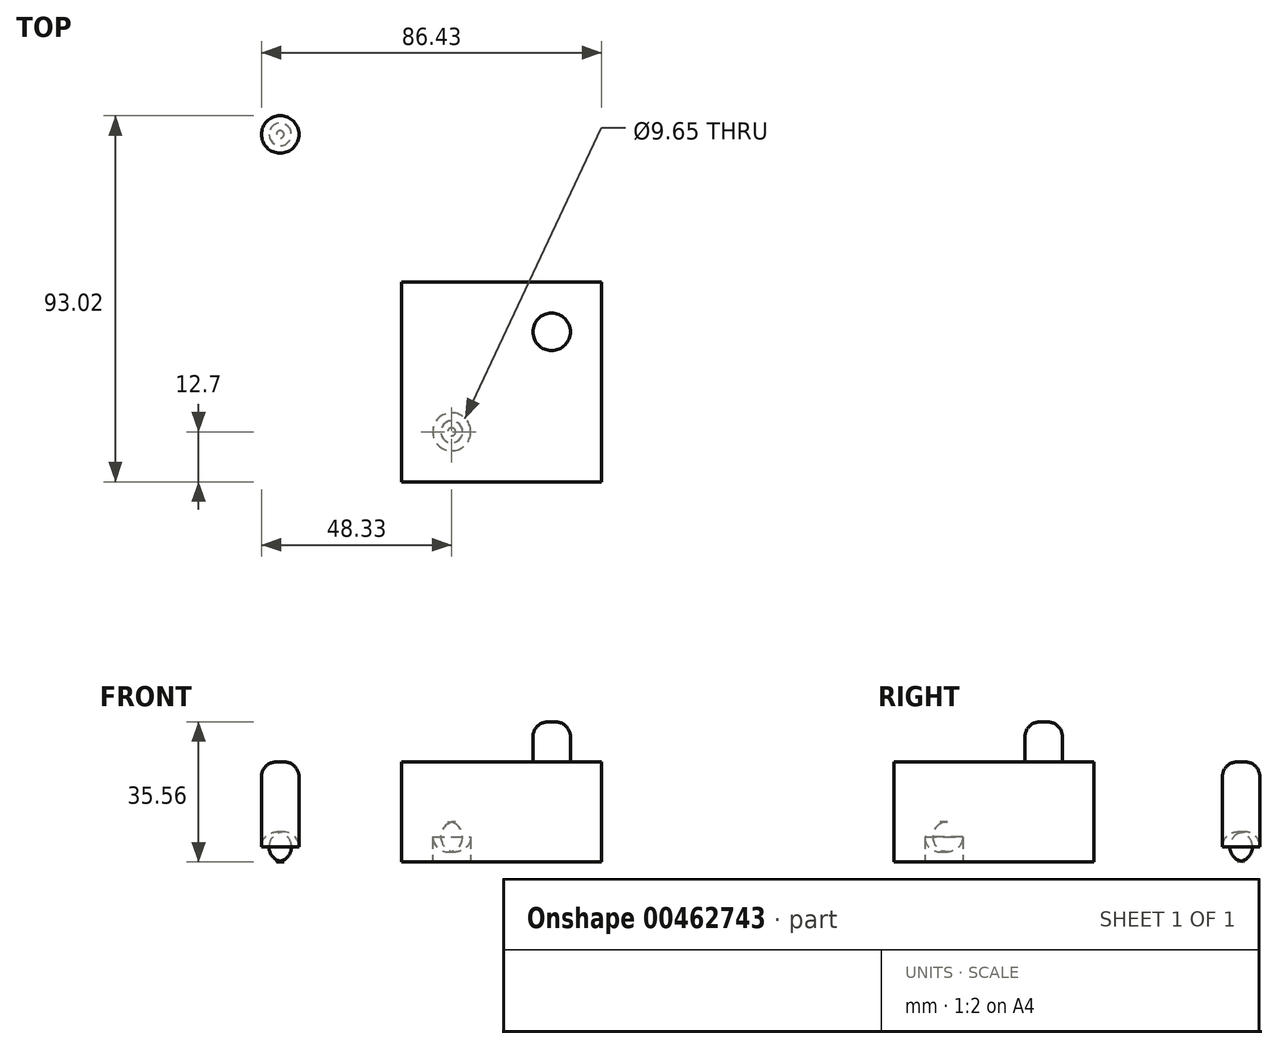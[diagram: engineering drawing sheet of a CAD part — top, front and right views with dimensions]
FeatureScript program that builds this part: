
annotation { "Feature Type Name" : "Feature", "Feature Type Description" : "" }
export const myFeature = defineFeature(function(context is Context, id is Id, definition is map)
    precondition{}
    {
        {
            var Q0;
            Q0=qCreatedBy(makeId("Top.planeOp"),FACE);
            var sketch = newSketch(context, id + "F0", { "sketchPlane" : qUnion([Q0])});
            skLineSegment(sketch, "E0.bottom", {"start": v(-25.4, -25.4) * mm, "end": v(25.4, -25.4) * mm});
            skLineSegment(sketch, "E0.top", {"start": v(-25.4, 25.4) * mm, "end": v(25.4, 25.4) * mm});
            skLineSegment(sketch, "E0.left", {"start": v(-25.4, -25.4) * mm, "end": v(-25.4, 25.4) * mm});
            skLineSegment(sketch, "E0.right", {"start": v(25.4, -25.4) * mm, "end": v(25.4, 25.4) * mm});
            skPoint(sketch, "E0.middle", {"position": v(0, 0) * mm});
            skSolve(sketch);
        }
        {
            var Q0;
            Q0=makeQuery(id+"F0.imprint","IMPRINT",FACE,{"disambiguationData":[TD([[makeQuery(id+"F0.imprint","IMPRINT",EDGE,{"derivedFrom":sQuery(id+"F0.wireOp",EDGE,"E0.bottom")}),1.0]])]});
            extrude(context, id + "F1", {"entities" : qUnion([Q0]), "depth" : 25.4 * mm});
        }
        {
            var Q0;
            Q0=makeQuery(id+"F1.opExtrude","CAP_FACE",FACE,{"disambiguationData":[OSD([sQuery(id+"F0.wireOp",EDGE,"E0.bottom"),sQuery(id+"F0.wireOp",EDGE,"E0.top"),sQuery(id+"F0.wireOp",EDGE,"E0.left"),sQuery(id+"F0.wireOp",EDGE,"E0.right")])],"isStart":false});
            var sketch = newSketch(context, id + "F2", { "sketchPlane" : qUnion([Q0])});
            skCircle(sketch, "E1", {"center": v(12.7, 12.7) * mm, "radius": 4.76 * mm});
            skSolve(sketch);
        }
        {
            var Q0;
            Q0=makeQuery(id+"F2.imprint","IMPRINT",FACE,{"disambiguationData":[TD([[makeQuery(id+"F2.imprint","IMPRINT",EDGE,{"derivedFrom":sQuery(id+"F2.wireOp",EDGE,"E1")}),1.0]])]});
            extrude(context, id + "F3", {"entities" : qUnion([Q0]), "operationType" : NewBodyOperationType.ADD, "depth" : 10.16 * mm});
        }
        {
            var Q0;
            Q0=makeQuery(id+"F3.opExtrude","CAP_EDGE",EDGE,{"disambiguationData":[OSD([sQuery(id+"F2.wireOp",EDGE,"E1")])],"isStart":false});
            fillet(context, id + "F4", {"entities" : qUnion([Q0]), "radius" : 3.8 * mm, "tangentPropagation" : true, "allowEdgeOverflow" : false});
        }
        {
            var Q0;
            Q0=makeQuery(id+"F1.opExtrude","CAP_FACE",FACE,{"disambiguationData":[OSD([sQuery(id+"F0.wireOp",EDGE,"E0.bottom"),sQuery(id+"F0.wireOp",EDGE,"E0.top"),sQuery(id+"F0.wireOp",EDGE,"E0.left"),sQuery(id+"F0.wireOp",EDGE,"E0.right")])],"isStart":true});
            var sketch = newSketch(context, id + "F5", { "sketchPlane" : qUnion([Q0])});
            skCircle(sketch, "E2", {"center": v(-12.7, 12.7) * mm, "radius": 4.83 * mm});
            skSolve(sketch);
        }
        {
            var Q0;
            Q0=makeQuery(id+"F5.imprint","IMPRINT",FACE,{"disambiguationData":[TD([[makeQuery(id+"F5.imprint","IMPRINT",EDGE,{"derivedFrom":sQuery(id+"F5.wireOp",EDGE,"E2")}),1.0]])]});
            extrude(context, id + "F6", {"entities" : qUnion([Q0]), "operationType" : NewBodyOperationType.REMOVE, "oppositeDirection" : true, "depth" : 10.16 * mm});
        }
        {
            var Q0;
            Q0=makeQuery(id+"F6.boolean.opBoolean","COPY",EDGE,{"derivedFrom":makeQuery(id+"F6.opExtrude","CAP_EDGE",EDGE,{"disambiguationData":[OSD([sQuery(id+"F5.wireOp",EDGE,"E2")])],"isStart":false})});
            fillet(context, id + "F7", {"entities" : qUnion([Q0]), "radius" : 3.8 * mm, "tangentPropagation" : true, "allowEdgeOverflow" : false});
        }
        {
            var Q0;
            Q0=qCreatedBy(makeId("Top.planeOp"),FACE);
            var sketch = newSketch(context, id + "F8", { "sketchPlane" : qUnion([Q0])});
            skCircle(sketch, "E3", {"center": v(-56.27, 62.86) * mm, "radius": 4.76 * mm});
            skSolve(sketch);
        }
        {
            var Q0;
            Q0=makeQuery(id+"F8.imprint","IMPRINT",FACE,{"disambiguationData":[TD([[makeQuery(id+"F8.imprint","IMPRINT",EDGE,{"derivedFrom":sQuery(id+"F8.wireOp",EDGE,"E3")}),1.0]])]});
            extrude(context, id + "F9", {"entities" : qUnion([Q0]), "depth" : 25.4 * mm});
        }
        {
            var Q0;
            Q0=makeQuery(id+"F9.opExtrude","CAP_EDGE",EDGE,{"disambiguationData":[OSD([sQuery(id+"F8.wireOp",EDGE,"E3")])],"isStart":false});
            var Q1;
            Q1=makeQuery(id+"F9.opExtrude","CAP_EDGE",EDGE,{"disambiguationData":[OSD([sQuery(id+"F8.wireOp",EDGE,"E3")])],"isStart":true});
            fillet(context, id + "F10", {"entities" : qUnion([Q0, Q1]), "radius" : 3.8 * mm, "tangentPropagation" : true, "allowEdgeOverflow" : false});
        }
    });
